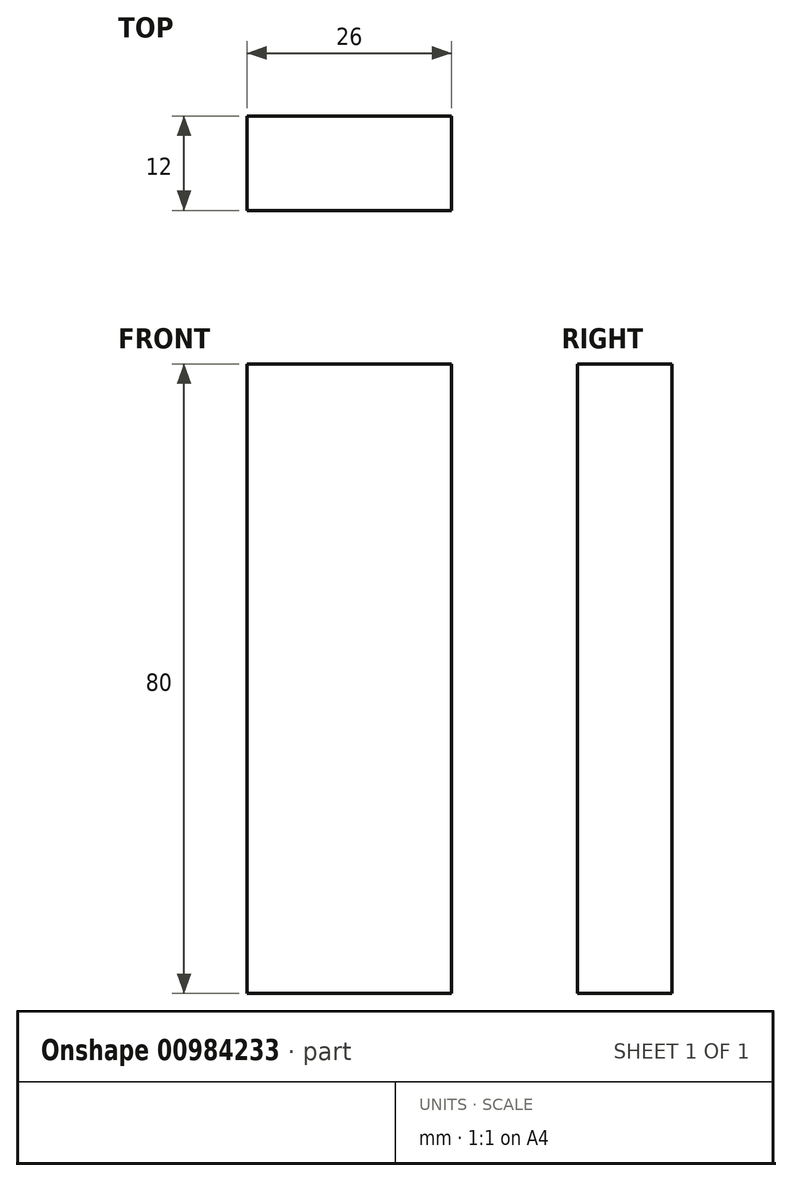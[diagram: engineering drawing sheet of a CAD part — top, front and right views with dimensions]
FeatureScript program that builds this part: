
annotation { "Feature Type Name" : "Feature", "Feature Type Description" : "" }
export const myFeature = defineFeature(function(context is Context, id is Id, definition is map)
    precondition{}
    {
        {
            var Q0;
            Q0=qCreatedBy(makeId("Front.planeOp"),FACE);
            var sketch = newSketch(context, id + "F0", { "sketchPlane" : qUnion([Q0])});
            skLineSegment(sketch, "E0.bottom", {"start": v(13, 40) * mm, "end": v(-13, 40) * mm});
            skLineSegment(sketch, "E0.top", {"start": v(13, -40) * mm, "end": v(-13, -40) * mm});
            skLineSegment(sketch, "E0.left", {"start": v(13, 40) * mm, "end": v(13, -40) * mm});
            skLineSegment(sketch, "E0.right", {"start": v(-13, 40) * mm, "end": v(-13, -40) * mm});
            skPoint(sketch, "E0.middle", {"position": v(0, 0) * mm});
            skSolve(sketch);
        }
        {
            var Q0;
            Q0=makeQuery(id+"F0.imprint","IMPRINT",FACE,{"disambiguationData":[TD([[makeQuery(id+"F0.imprint","IMPRINT",EDGE,{"derivedFrom":sQuery(id+"F0.wireOp",EDGE,"E0.bottom")}),1.0]])]});
            extrude(context, id + "F1", {"entities" : qUnion([Q0]), "oppositeDirection" : true, "depth" : 12 * mm, "offsetDistance" : 25 * mm});
        }
    });
